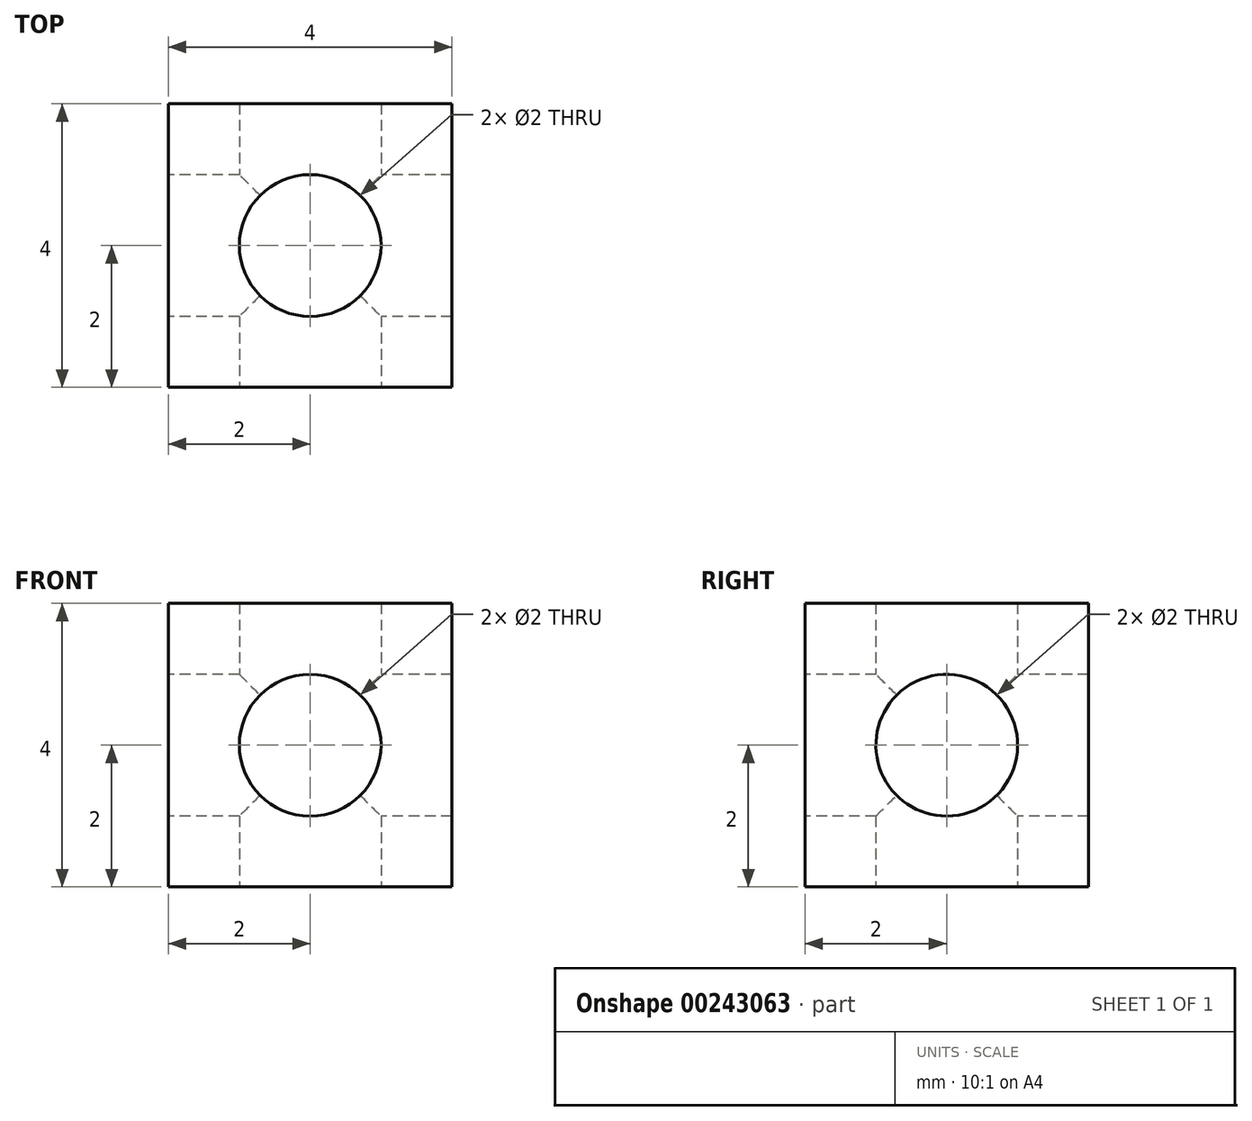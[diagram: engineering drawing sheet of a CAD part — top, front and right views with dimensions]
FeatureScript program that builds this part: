
annotation { "Feature Type Name" : "Feature", "Feature Type Description" : "" }
export const myFeature = defineFeature(function(context is Context, id is Id, definition is map)
    precondition{}
    {
        {
            var Q0;
            Q0=qCreatedBy(makeId("Front.planeOp"),FACE);
            var sketch = newSketch(context, id + "F0", { "sketchPlane" : qUnion([Q0])});
            skLineSegment(sketch, "E0.bottom", {"start": v(0, 0) * mm, "end": v(4, 0) * mm});
            skLineSegment(sketch, "E0.top", {"start": v(0, 4) * mm, "end": v(4, 4) * mm});
            skLineSegment(sketch, "E0.left", {"start": v(0, 0) * mm, "end": v(0, 4) * mm});
            skLineSegment(sketch, "E0.right", {"start": v(4, 0) * mm, "end": v(4, 4) * mm});
            skSolve(sketch);
        }
        {
            var Q0;
            Q0 = qSketchRegion(id + "F0", true);
            extrude(context, id + "F1", {"entities" : qUnion([Q0]), "oppositeDirection" : true, "depth" : 4 * mm});
        }
        {
            var Q0;
            Q0=makeQuery(id+"F1.opExtrude","CAP_FACE",FACE,{"disambiguationData":[OSD([sQuery(id+"F0.wireOp",EDGE,"E0.bottom"),sQuery(id+"F0.wireOp",EDGE,"E0.top"),sQuery(id+"F0.wireOp",EDGE,"E0.left"),sQuery(id+"F0.wireOp",EDGE,"E0.right")])],"isStart":true});
            var sketch = newSketch(context, id + "F2", { "sketchPlane" : qUnion([Q0])});
            skLineSegment(sketch, "E1", {"start": v(2, 4) * mm, "end": v(2, 2) * mm, "construction": true});
            skPoint(sketch, "E1.endSnap0", {"position": v(2, 4) * mm});
            skCircle(sketch, "E2", {"center": v(2, 2) * mm, "radius": 1 * mm});
            skSolve(sketch);
        }
        {
            var Q0;
            Q0=makeQuery(id+"F2.imprint","IMPRINT",FACE,{"disambiguationData":[TD([[makeQuery(id+"F2.imprint","IMPRINT",EDGE,{"derivedFrom":sQuery(id+"F2.wireOp",EDGE,"E2")}),1.0]])]});
            var Q1;
            Q1=sQuery(id+"F2.wireOp",EDGE,"E2");
            extrude(context, id + "F3", {"entities" : qUnion([Q0]), "operationType" : NewBodyOperationType.REMOVE, "surfaceEntities" : qUnion([Q1]), "oppositeDirection" : true, "depth" : 25 * mm});
        }
        {
            var Q0;
            Q0=qCreatedBy(makeId("Top.planeOp"),FACE);
            var sketch = newSketch(context, id + "F4", { "sketchPlane" : qUnion([Q0])});
            skLineSegment(sketch, "E3", {"start": v(0, 0) * mm, "end": v(2, 0) * mm, "construction": true});
            skLineSegment(sketch, "E4", {"start": v(2, 0) * mm, "end": v(2, 2) * mm, "construction": true});
            skCircle(sketch, "E5", {"center": v(2, 2) * mm, "radius": 1 * mm});
            skSolve(sketch);
        }
        {
            var Q0;
            Q0=makeQuery(id+"F4.imprint","IMPRINT",FACE,{"disambiguationData":[TD([[makeQuery(id+"F4.imprint","IMPRINT",EDGE,{"derivedFrom":sQuery(id+"F4.wireOp",EDGE,"E5")}),1.0]])]});
            var Q1;
            Q1=sQuery(id+"F4.wireOp",EDGE,"E5");
            extrude(context, id + "F5", {"entities" : qUnion([Q0]), "operationType" : NewBodyOperationType.REMOVE, "surfaceEntities" : qUnion([Q1]), "depth" : 25 * mm});
        }
        {
            var Q0;
            Q0=makeQuery(id+"F1.opExtrude","SWEPT_FACE",FACE,{"disambiguationData":[OSD([sQuery(id+"F0.wireOp",EDGE,"E0.left")])]});
            var sketch = newSketch(context, id + "F6", { "sketchPlane" : qUnion([Q0])});
            skLineSegment(sketch, "E6", {"start": v(-2, 0) * mm, "end": v(-2, 2) * mm, "construction": true});
            skCircle(sketch, "E7", {"center": v(-2, 2) * mm, "radius": 1 * mm});
            skSolve(sketch);
        }
        {
            var Q0;
            Q0=makeQuery(id+"F6.imprint","IMPRINT",FACE,{"disambiguationData":[TD([[makeQuery(id+"F6.imprint","IMPRINT",EDGE,{"derivedFrom":sQuery(id+"F6.wireOp",EDGE,"E7")}),1.0]])]});
            var Q1;
            Q1=sQuery(id+"F6.wireOp",EDGE,"E7");
            extrude(context, id + "F7", {"entities" : qUnion([Q0]), "operationType" : NewBodyOperationType.REMOVE, "surfaceEntities" : qUnion([Q1]), "oppositeDirection" : true, "depth" : 25 * mm});
        }
    });
